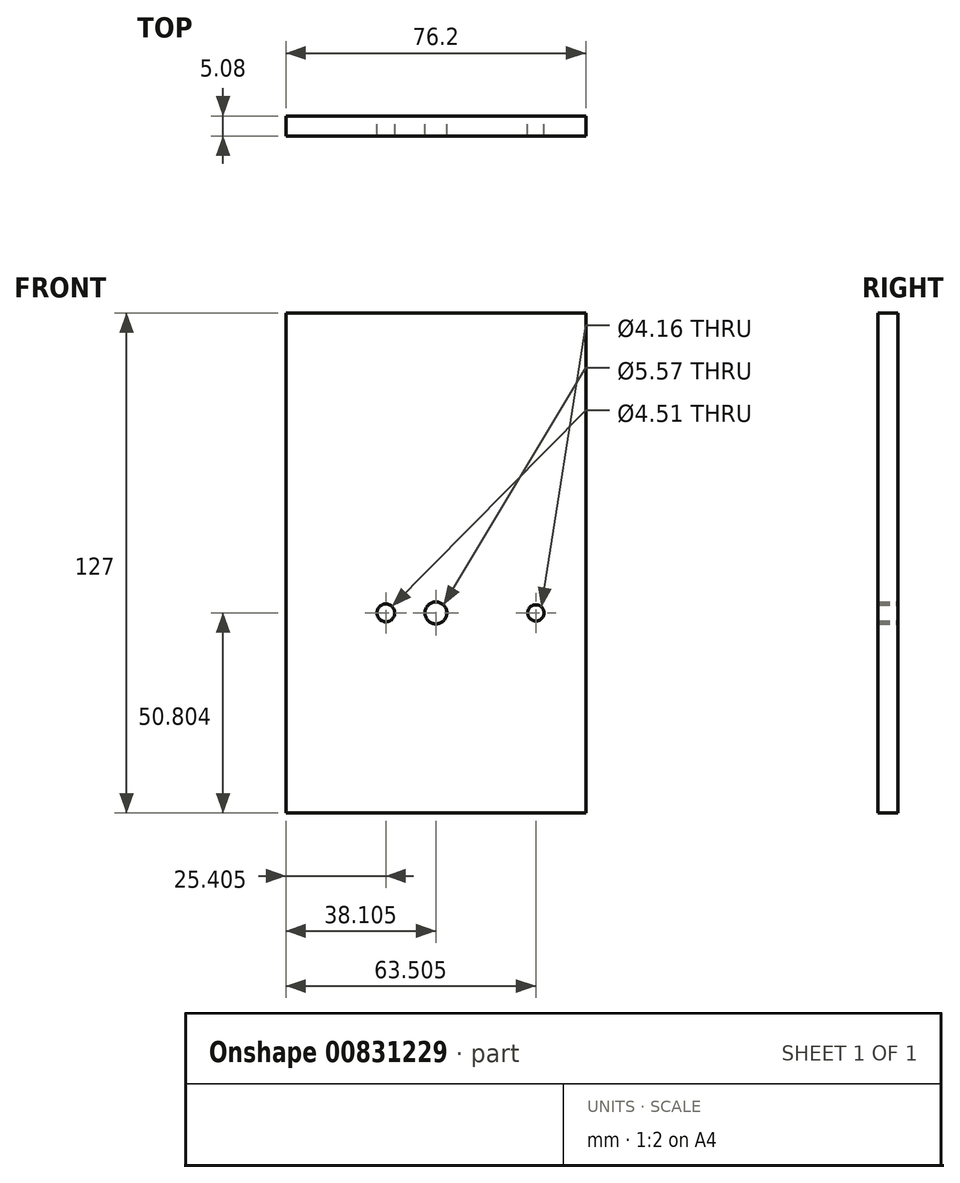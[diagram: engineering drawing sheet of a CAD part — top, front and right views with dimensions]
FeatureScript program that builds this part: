
annotation { "Feature Type Name" : "Feature", "Feature Type Description" : "" }
export const myFeature = defineFeature(function(context is Context, id is Id, definition is map)
    precondition{}
    {
        {
            var Q0;
            Q0=qCreatedBy(makeId("Front.planeOp"),FACE);
            var sketch = newSketch(context, id + "F0", { "sketchPlane" : qUnion([Q0])});
            skLineSegment(sketch, "E0.bottom", {"start": v(-39.25, 10.86) * mm, "end": v(36.95, 10.86) * mm});
            skLineSegment(sketch, "E0.top", {"start": v(-39.25, -116.14) * mm, "end": v(36.95, -116.14) * mm});
            skLineSegment(sketch, "E0.left", {"start": v(-39.25, 10.86) * mm, "end": v(-39.25, -116.14) * mm});
            skLineSegment(sketch, "E0.right", {"start": v(36.95, 10.86) * mm, "end": v(36.95, -116.14) * mm});
            skCircle(sketch, "E1", {"center": v(24.25, -65.34) * mm, "radius": 2.08 * mm});
            skCircle(sketch, "E2", {"center": v(-1.15, -65.34) * mm, "radius": 2.78 * mm});
            skCircle(sketch, "E3", {"center": v(-13.85, -65.34) * mm, "radius": 2.25 * mm});
            skSolve(sketch);
        }
        {
            var Q0;
            Q0=makeQuery(id+"F0.imprint","IMPRINT",FACE,{"disambiguationData":[TD([[makeQuery(id+"F0.imprint","IMPRINT",EDGE,{"derivedFrom":sQuery(id+"F0.wireOp",EDGE,"E0.bottom")}),-1.0]])]});
            extrude(context, id + "F1", {"entities" : qUnion([Q0]), "depth" : 5.08 * mm, "offsetDistance" : 25.4 * mm});
        }
    });
